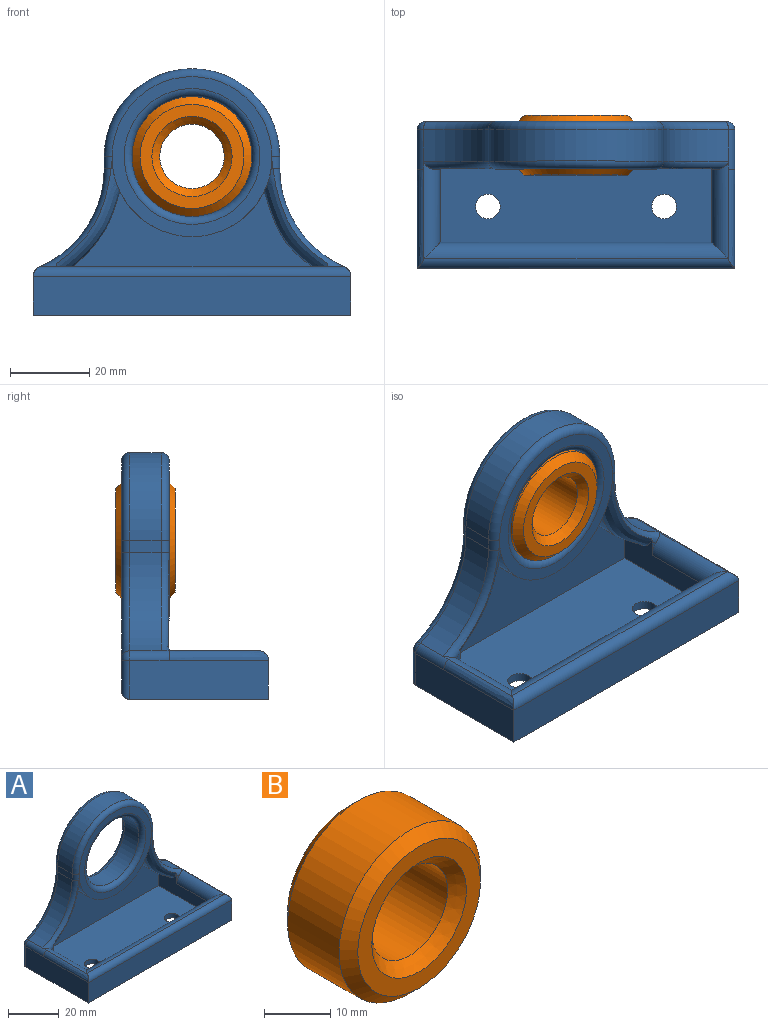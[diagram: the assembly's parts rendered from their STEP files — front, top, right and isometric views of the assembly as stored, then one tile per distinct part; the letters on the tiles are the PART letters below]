
ASSEMBLY  parts=2 mates=1
PART A: 51 faces, bbox 81x38x64.9 mm
  f0: plane 4.11x1.54mm, normal (0,-1,0), area 2.2mm2, adj f21,f24,f30
  f1: plane 40.29x40.2mm, normal (0,-1,0), area 356.3mm2, adj f27,f28,f29,f42,f44
  f2: plane 4.11x1.54mm, normal (0,-1,0), area 2.2mm2, adj f19,f23,f26
  f3: cylinder r=26.97mm len=24.77mm, axis (0,1,0), area 251.2mm2, adj f4,f12,f26,f39
  f4: cylinder r=2.64mm len=10mm, axis (0,1,0), area 30.7mm2, adj f3,f5,f15,f23,f37
  f5: plane 35x9.78mm, normal (-1,0,0), area 342.2mm2, adj f4,f6,f15,f17,f35
  f6: plane 80x35mm, normal (0,0,-1), area 2739.6mm2, adj f5,f7,f17,f33,f49,f50
  f7: plane 35x9.78mm, normal (1,0,0), area 342.2mm2, adj f6,f8,f16,f17,f31
  f8: cylinder r=2.64mm len=10mm, axis (0,1,0), area 30.7mm2, adj f7,f9,f16,f24,f32
  f9: cylinder r=26.97mm len=24.77mm, axis (0,1,0), area 251.2mm2, adj f8,f10,f30,f34
  f10: plane 8x3.03mm, normal (1,0,0), area 24.3mm2, adj f9,f11,f29,f36
  f11: cylinder r=22.1mm len=44.2mm, axis (0,1,0), area 555.4mm2, adj f10,f12,f28,f38
  f12: plane 8x3.03mm, normal (-1,0,0), area 24.3mm2, adj f3,f11,f27,f40
  f13: cylinder r=15.1mm len=30.2mm, axis (0,1,0), area 759mm2, adj f41,f42
  f14: plane 76x58.1mm, normal (0,1,0), area 1802.5mm2, adj f31,f32,f33,f34,f35,f36,f37,f38
  f15: extruded ~25x2.42mm, area 74.7mm2, adj f4,f5,f17,f18,f23
  f16: extruded ~25x2.42mm, area 74.7mm2, adj f7,f8,f17,f18,f24
  f17: plane 80x9.78mm, normal (0,-1,0), area 782.2mm2, adj f5,f6,f7,f15,f16,f18
  f18: cylinder r=2.42mm len=80mm, axis (1,0,0), area 298mm2, adj f15,f16,f17,f25
  f19: plane 29.39x11.81mm, normal (1,0,0), area 181.4mm2, adj f2,f20,f22,f23,f26,f45,f46,f48
  f20: plane 68.41x5.8mm, normal (0,1,0), area 396.8mm2, adj f19,f21,f22,f25
  f21: plane 29.38x11.82mm, normal (-1,0,0), area 181.5mm2, adj f0,f20,f22,f24,f30,f43,f46,f47
  f22: plane 68.41x28.38mm, normal (0,0,1), area 1881.2mm2, adj f19,f20,f21,f46,f49,f50
  f23: cylinder r=4.2mm len=24.58mm, axis (0,1,0), area 138mm2, adj f2,f4,f15,f19,f25,f26
  f24: cylinder r=4.2mm len=24.58mm, axis (0,-1,0), area 138mm2, adj f0,f8,f16,f21,f25,f30
  f25: cylinder r=4.2mm len=76.81mm, axis (-1,0,0), area 479.1mm2, adj f18,f20,f23,f24
  f26: torus R=28.97mm, axis (0,-1,0), area 75.8mm2, adj f2,f3,f19,f23,f27,f48
  f27: cylinder r=2mm len=3.03mm, axis (0,0,1), area 9.2mm2, adj f1,f12,f26,f28,f44,f48
  f28: torus R=20.1mm, axis (0,-1,0), area 210.9mm2, adj f1,f11,f27,f29
  f29: cylinder r=2mm len=3.03mm, axis (0,0,-1), area 9.2mm2, adj f1,f10,f28,f30,f44,f47
  f30: torus R=28.97mm, axis (0,-1,0), area 76.7mm2, adj f0,f9,f21,f24,f29,f47
  f31: cylinder r=2mm len=9.78mm, axis (0,0,1), area 27.6mm2, adj f7,f14,f32,f33
  f32: torus R=0.64mm, axis (0,-1,0), area 7mm2, adj f8,f14,f31,f34
  f33: cylinder r=2mm len=80mm, axis (1,0,0), area 245mm2, adj f6,f14,f31,f35
  f34: torus R=28.97mm, axis (0,-1,0), area 101.3mm2, adj f9,f14,f32,f36
  f35: cylinder r=2mm len=9.78mm, axis (0,0,-1), area 27.6mm2, adj f5,f14,f33,f37
  f36: cylinder r=2mm len=3.03mm, axis (0,0,1), area 9.5mm2, adj f10,f14,f34,f38
  f37: torus R=0.64mm, axis (0,-1,0), area 7mm2, adj f4,f14,f35,f39
  f38: torus R=20.1mm, axis (0,-1,0), area 210.9mm2, adj f11,f14,f36,f40
  f39: torus R=28.97mm, axis (0,-1,0), area 101.3mm2, adj f3,f14,f37,f40
  f40: cylinder r=2mm len=3.03mm, axis (0,0,-1), area 9.5mm2, adj f12,f14,f38,f39
  f41: torus R=17.1mm, axis (0,-1,0), area 312.4mm2, adj f13,f14
  f42: torus R=17.1mm, axis (0,-1,0), area 312.4mm2, adj f1,f13
  f43: extruded ~21.91x16.06mm, area 162.3mm2, adj f21,f44,f46,f47
  f44: cylinder r=20.19mm len=40.32mm, axis (0,-1,0), area 463.2mm2, adj f1,f27,f29,f43,f45,f46,f47,f48
  f45: extruded ~21.91x16.06mm, area 161.8mm2, adj f19,f44,f46,f48
  f46: plane 68.41x28.94mm, normal (0,-1,0), area 1232.1mm2, adj f19,f21,f22,f43,f44,f45
  f47: bspline ~33.2x22.77mm, area 160.9mm2, adj f21,f29,f30,f43,f44
  f48: bspline ~40.2x24.33mm, area 160.8mm2, adj f19,f26,f27,f44,f45
  f49: cylinder r=3.1mm len=6.2mm, axis (0,0,1), area 42.8mm2, adj f6,f22
  f50: cylinder r=3.1mm len=6.2mm, axis (0,0,1), area 42.8mm2, adj f6,f22
PART B: 8 faces, bbox 30.2x15x30.2 mm
  f0: cylinder r=8.1mm len=16.2mm, axis (0,1,0), area 559.8mm2, adj f4,f7
  f1: cylinder r=15.1mm len=30.2mm, axis (0,1,0), area 1043.6mm2, adj f5,f6
  f2: plane 26.2x26.2mm, normal (0,-1,0), area 218.7mm2, adj f4,f5
  f3: plane 26.2x26.2mm, normal (0,1,0), area 218.7mm2, adj f6,f7
  f4: cone r=8.1mm half-angle=45deg, axis (0,-1,0), area 161.7mm2, adj f0,f2
  f5: cone r=13.1mm half-angle=45deg, axis (0,1,0), area 250.6mm2, adj f1,f2
  f6: cone r=15.1mm half-angle=45deg, axis (0,-1,0), area 250.6mm2, adj f1,f3
  f7: cone r=10.1mm half-angle=45deg, axis (0,1,0), area 161.7mm2, adj f0,f3
PLACE A t=(-43.55,-30.45,-26.78)mm
PLACE B t=(-43.55,-28.95,-26.78)mm
MATE fastened B.f1 <-> A.f13  axis (0,1,0) through (-43.55,-36.45,-26.78)mm
